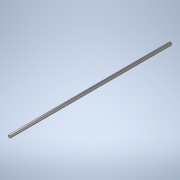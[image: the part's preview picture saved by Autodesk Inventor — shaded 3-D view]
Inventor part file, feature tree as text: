
AUTODESK INVENTOR PART (.ipt)
format: ipt  version: 2020 (Build 240168000, 168)  size: 109,568 bytes
history: native  units: in
note: dims shown in document units (in); Inventor stores cm internally (conversion verified against a paired STEP export)
features: extrude x1, sketch x1
ambient origin geometry x8: Origin, YZ Plane, XZ Plane, XY Plane, X Axis, Y Axis, Z Axis, Center Point
bodies: Solid1 (feature_tree)
feature tree (2):
  extrude  "Extrusion1"  Depth=32.0in TaperAngle=0.0deg
  sketch  "Sketch1"  dims[d0=0.5in d1=32.0in d2=0.0in]
